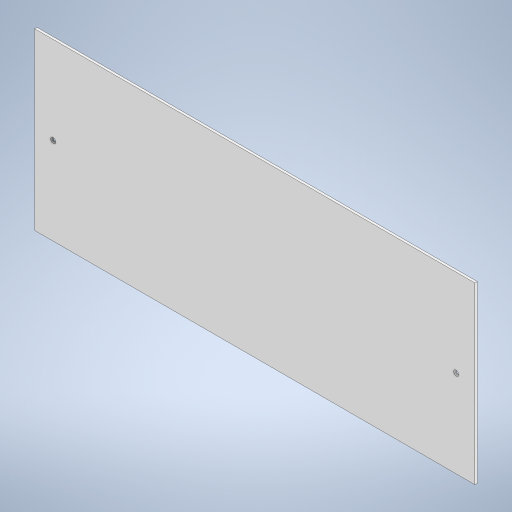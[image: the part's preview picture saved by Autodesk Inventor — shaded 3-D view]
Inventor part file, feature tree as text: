
AUTODESK INVENTOR PART (.ipt)
format: ipt  version: 2023 (Build 270158000, 158)  size: 203,776 bytes
history: native  units: mm
features: sketch x2, extrude x1, hole x1
ambient origin geometry x8: Origin, YZ Plane, XZ Plane, XY Plane, X Axis, Y Axis, Z Axis, Center Point
bodies: Solid1 (feature_tree)
feature tree (4):
  extrude  "Extrusion1"  Depth=215.0mm
  hole  "Hole1"  [1 undecoded]
  sketch  "Sketch1"  dims[d0=542.0mm d1=215.0mm]
  sketch  "Sketch2"  dims[d2=3.0mm d3=0.0mm d4=23.0mm d5=23.0mm d6=6.5mm d7=6.0mm d8=4.0mm d9=2.0mm d10=90.0deg d11=8.0mm d12=20.594885mm]
note: 1 required parameter value undecoded (feature->parameter linkage not recoverable at this tier; creation-order binding heuristic only, values carry confidence <= 0.55)
